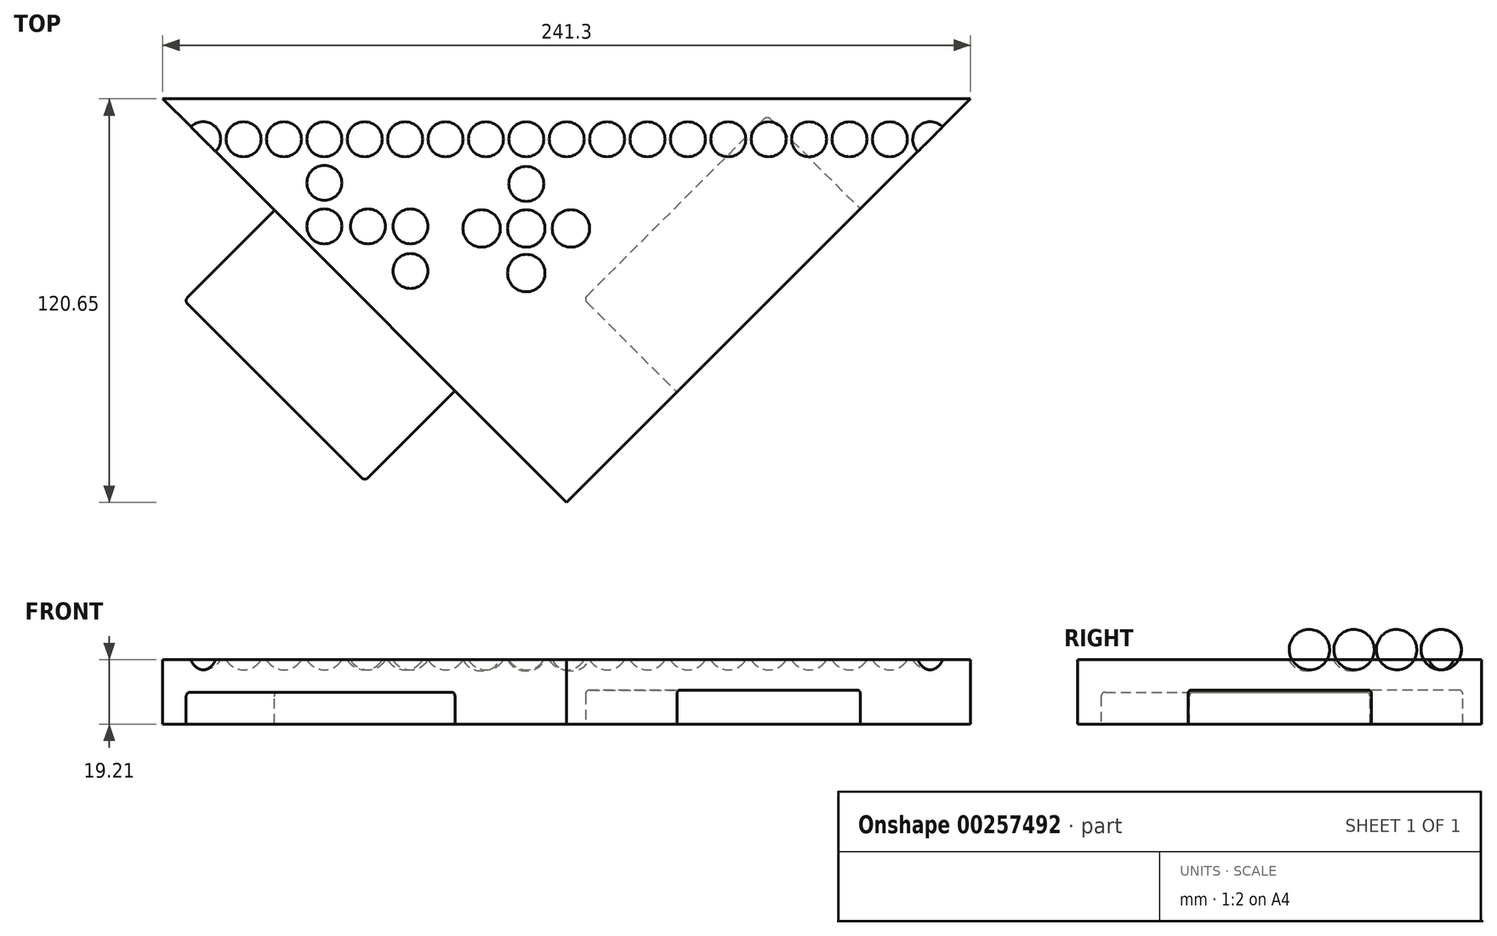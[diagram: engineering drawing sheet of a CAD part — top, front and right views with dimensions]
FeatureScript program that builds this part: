
annotation { "Feature Type Name" : "Feature", "Feature Type Description" : "" }
export const myFeature = defineFeature(function(context is Context, id is Id, definition is map)
    precondition{}
    {
        {
            var Q0;
            Q0=qCreatedBy(makeId("Top.planeOp"),FACE);
            var sketch = newSketch(context, id + "F0", { "sketchPlane" : qUnion([Q0])});
            skLineSegment(sketch, "E0.bottom", {"start": v(120.65, -120.65) * mm, "end": v(-120.65, -120.65) * mm});
            skLineSegment(sketch, "E0.top", {"start": v(120.65, 120.65) * mm, "end": v(-120.65, 120.65) * mm});
            skLineSegment(sketch, "E0.left", {"start": v(120.65, -120.65) * mm, "end": v(120.65, 120.65) * mm});
            skLineSegment(sketch, "E0.right", {"start": v(-120.65, -120.65) * mm, "end": v(-120.65, 120.65) * mm});
            skPoint(sketch, "E0.middle", {"position": v(0, 0) * mm});
            skSolve(sketch);
        }
        {
            var Q0;
            Q0=makeQuery(id+"F0.imprint","IMPRINT",FACE,{"disambiguationData":[TD([[makeQuery(id+"F0.imprint","IMPRINT",EDGE,{"derivedFrom":sQuery(id+"F0.wireOp",EDGE,"E0.bottom")}),-1.0]])]});
            extrude(context, id + "F1", {"entities" : qUnion([Q0]), "depth" : 19.05 * mm});
        }
        {
            var Q0;
            Q0=makeQuery(id+"F1.opExtrude","CAP_FACE",FACE,{"disambiguationData":[OSD([sQuery(id+"F0.wireOp",EDGE,"E0.bottom"),sQuery(id+"F0.wireOp",EDGE,"E0.top"),sQuery(id+"F0.wireOp",EDGE,"E0.left"),sQuery(id+"F0.wireOp",EDGE,"E0.right")])],"isStart":false});
            var sketch = newSketch(context, id + "F2", { "sketchPlane" : qUnion([Q0])});
            skLineSegment(sketch, "E1", {"start": v(120.65, 120.65) * mm, "end": v(0, 0) * mm});
            skLineSegment(sketch, "E2", {"start": v(0, 0) * mm, "end": v(-120.65, 120.65) * mm});
            skLineSegment(sketch, "E3", {"start": v(-120.65, 120.65) * mm, "end": v(-120.65, -120.65) * mm});
            skLineSegment(sketch, "E4", {"start": v(-120.65, -120.65) * mm, "end": v(120.65, -120.65) * mm});
            skLineSegment(sketch, "E5", {"start": v(120.65, -120.65) * mm, "end": v(120.65, 120.65) * mm});
            skSolve(sketch);
        }
        {
            var Q0;
            Q0 = qSketchRegion(id + "F2", true);
            extrude(context, id + "F3", {"entities" : qUnion([Q0]), "operationType" : NewBodyOperationType.REMOVE, "endBound" : BoundingType.THROUGH_ALL, "oppositeDirection" : true, "depth" : 25.4 * mm});
        }
        {
            var Q0;
            Q0=makeQuery(id+"F3.boolean.opBoolean","COPY",FACE,{"derivedFrom":makeQuery(id+"F3.opExtrude","SWEPT_FACE",FACE,{"disambiguationData":[OSD([sQuery(id+"F2.wireOp",EDGE,"E1")])]})});
            var sketch = newSketch(context, id + "F4", { "sketchPlane" : qUnion([Q0])});
            skLineSegment(sketch, "E6.bottom", {"start": v(124.05, 10.16) * mm, "end": v(46.58, 10.16) * mm});
            skLineSegment(sketch, "E6.top", {"start": v(124.05, -10.16) * mm, "end": v(46.58, -10.16) * mm});
            skLineSegment(sketch, "E6.left", {"start": v(124.05, 10.16) * mm, "end": v(124.05, -10.16) * mm});
            skLineSegment(sketch, "E6.right", {"start": v(46.58, 10.16) * mm, "end": v(46.58, -10.16) * mm});
            skPoint(sketch, "E6.middle", {"position": v(85.31, 0) * mm});
            skSolve(sketch);
        }
        {
            var Q0;
            Q0 = qSketchRegion(id + "F4", true);
            extrude(context, id + "F5", {"entities" : qUnion([Q0]), "operationType" : NewBodyOperationType.REMOVE, "oppositeDirection" : true, "depth" : 39.37 * mm});
        }
        {
            var Q0;
            Q0=makeQuery(id+"F3.boolean.opBoolean","COPY",FACE,{"derivedFrom":makeQuery(id+"F3.opExtrude","SWEPT_FACE",FACE,{"disambiguationData":[OSD([sQuery(id+"F2.wireOp",EDGE,"E2")])]})});
            var sketch = newSketch(context, id + "F6", { "sketchPlane" : qUnion([Q0])});
            skLineSegment(sketch, "E7.bottom", {"start": v(-47.21, -9.53) * mm, "end": v(-123.41, -9.52) * mm});
            skLineSegment(sketch, "E7.top", {"start": v(-47.21, 9.52) * mm, "end": v(-123.41, 9.53) * mm});
            skLineSegment(sketch, "E7.left", {"start": v(-47.21, -9.53) * mm, "end": v(-47.21, 9.53) * mm});
            skLineSegment(sketch, "E7.right", {"start": v(-123.41, -9.52) * mm, "end": v(-123.41, 9.53) * mm});
            skPoint(sketch, "E7.middle", {"position": v(-85.31, 0) * mm});
            skSolve(sketch);
        }
        {
            var Q0;
            {var subQ0=sQuery(id+"F6.wireOp",EDGE,"E7.top");Q0=makeQuery(id+"F6.imprint","IMPRINT",FACE,{"disambiguationData":[TD([[makeQuery(id+"F6.imprint","IMPRINT",EDGE,{"derivedFrom":subQ0}),1.0]])]});}
            extrude(context, id + "F7", {"entities" : qUnion([Q0]), "operationType" : NewBodyOperationType.ADD, "depth" : 38.1 * mm});
        }
        {
            var Q0;
            Q0=makeQuery(id+"F7.opExtrude","CAP_EDGE",EDGE,{"disambiguationData":[OSD([sQuery(id+"F6.wireOp",EDGE,"E7.left")])],"isStart":true});
            var Q1;
            Q1=makeQuery(id+"F7.opExtrude","CAP_EDGE",EDGE,{"disambiguationData":[OSD([sQuery(id+"F6.wireOp",EDGE,"E7.top")])],"isStart":true});
            var Q2;
            Q2=makeQuery(id+"F7.opExtrude","CAP_EDGE",EDGE,{"disambiguationData":[OSD([sQuery(id+"F6.wireOp",EDGE,"E7.right")])],"isStart":true});
            var Q3;
            Q3=makeQuery(id+"F5.boolean.opBoolean","COPY",EDGE,{"derivedFrom":makeQuery(id+"F5.opExtrude","CAP_EDGE",EDGE,{"disambiguationData":[OSD([sQuery(id+"F4.wireOp",EDGE,"E6.right")])],"isStart":false})});
            var Q4;
            Q4=makeQuery(id+"F5.boolean.opBoolean","COPY",EDGE,{"derivedFrom":makeQuery(id+"F5.opExtrude","CAP_EDGE",EDGE,{"disambiguationData":[OSD([sQuery(id+"F4.wireOp",EDGE,"E6.bottom")])],"isStart":false})});
            var Q5;
            Q5=makeQuery(id+"F5.boolean.opBoolean","COPY",EDGE,{"derivedFrom":makeQuery(id+"F5.opExtrude","CAP_EDGE",EDGE,{"disambiguationData":[OSD([sQuery(id+"F4.wireOp",EDGE,"E6.left")])],"isStart":false})});
            var Q6;
            Q6=makeQuery(id+"F5.boolean.opBoolean","COPY",EDGE,{"derivedFrom":makeQuery(id+"F5.opExtrude","SWEPT_EDGE",EDGE,{"disambiguationData":[OSD([sQuery(id+"F4.wireOp",EDGE,"E6.bottom"),sQuery(id+"F4.wireOp",EDGE,"E6.left")])]})});
            var Q7;
            Q7=makeQuery(id+"F5.boolean.opBoolean","COPY",EDGE,{"derivedFrom":makeQuery(id+"F5.opExtrude","SWEPT_EDGE",EDGE,{"disambiguationData":[OSD([sQuery(id+"F4.wireOp",EDGE,"E6.bottom"),sQuery(id+"F4.wireOp",EDGE,"E6.right")])]})});
            fillet(context, id + "F8", {"entities" : qUnion([Q0, Q1, Q2, Q3, Q4, Q5, Q6, Q7]), "radius" : 1.27 * mm, "tangentPropagation" : true, "allowEdgeOverflow" : false});
        }
        {
            var Q0;
            Q0=makeQuery(id+"F7.opExtrude","SWEPT_EDGE",EDGE,{"disambiguationData":[OSD([sQuery(id+"F6.wireOp",EDGE,"E7.top"),sQuery(id+"F6.wireOp",EDGE,"E7.left")])]});
            var Q1;
            Q1=makeQuery(id+"F7.opExtrude","CAP_EDGE",EDGE,{"disambiguationData":[OSD([sQuery(id+"F6.wireOp",EDGE,"E7.left")])],"isStart":false});
            var Q2;
            Q2=makeQuery(id+"F7.opExtrude","CAP_EDGE",EDGE,{"disambiguationData":[OSD([sQuery(id+"F6.wireOp",EDGE,"E7.top")])],"isStart":false});
            var Q3;
            Q3=makeQuery(id+"F7.opExtrude","CAP_EDGE",EDGE,{"disambiguationData":[OSD([sQuery(id+"F6.wireOp",EDGE,"E7.right")])],"isStart":false});
            var Q4;
            Q4=makeQuery(id+"F7.opExtrude","SWEPT_EDGE",EDGE,{"disambiguationData":[OSD([sQuery(id+"F6.wireOp",EDGE,"E7.top"),sQuery(id+"F6.wireOp",EDGE,"E7.right")])]});
            var Q5;
            Q5=makeQuery(id+"F5.boolean.opBoolean","COPY",EDGE,{"derivedFrom":makeQuery(id+"F5.opExtrude","CAP_EDGE",EDGE,{"disambiguationData":[OSD([sQuery(id+"F4.wireOp",EDGE,"E6.left")])],"isStart":true})});
            fillet(context, id + "F9", {"entities" : qUnion([Q0, Q1, Q2, Q3, Q4, Q5]), "radius" : 1.27 * mm, "tangentPropagation" : true, "allowEdgeOverflow" : false});
        }
        {
            var Q0;
            Q0=makeQuery(id+"F1.opExtrude","CAP_FACE",FACE,{"disambiguationData":[OSD([sQuery(id+"F0.wireOp",EDGE,"E0.bottom"),sQuery(id+"F0.wireOp",EDGE,"E0.top"),sQuery(id+"F0.wireOp",EDGE,"E0.left"),sQuery(id+"F0.wireOp",EDGE,"E0.right")])],"isStart":false});
            var sketch = newSketch(context, id + "F10", { "sketchPlane" : qUnion([Q0])});
            skLineSegment(sketch, "E8", {"start": v(-120.65, 120.65) * mm, "end": v(120.65, 120.65) * mm});
            skLineSegment(sketch, "E9", {"start": v(120.65, 120.65) * mm, "end": v(0, 0) * mm});
            skLineSegment(sketch, "E10", {"start": v(0, 0) * mm, "end": v(-120.65, 120.65) * mm});
            skSolve(sketch);
        }
        {
            var Q0;
            Q0 = qSketchRegion(id + "F10", true);
            extrude(context, id + "F11", {"entities" : qUnion([Q0]), "operationType" : NewBodyOperationType.ADD, "depth" : 3.17 * mm});
        }
        {
            var Q0;
            Q0=makeQuery(id+"F11.opExtrude","CAP_FACE",FACE,{"disambiguationData":[OSD([sQuery(id+"F10.wireOp",EDGE,"E8"),sQuery(id+"F10.wireOp",EDGE,"E9"),sQuery(id+"F10.wireOp",EDGE,"E10")])],"isStart":false});
            var sketch = newSketch(context, id + "F12", { "sketchPlane" : qUnion([Q0])});
            skCircle(sketch, "E11", {"center": v(0, 111.12) * mm, "radius": 6.35 * mm});
            skSolve(sketch);
        }
        {
            var Q0;
            Q0=makeQuery(id+"F12.imprint","IMPRINT",FACE,{"disambiguationData":[TD([[makeQuery(id+"F12.imprint","IMPRINT",EDGE,{"derivedFrom":sQuery(id+"F12.wireOp",EDGE,"E11")}),-1.0]])]});
            var sketch = newSketch(context, id + "F13", { "sketchPlane" : qUnion([Q0])});
            skLineSegment(sketch, "E12", {"start": v(0, 120.94) * mm, "end": v(0, 0) * mm});
            skSolve(sketch);
        }
        {
            var Q0;
            {var subQ0=makeQuery(id+"F12.imprint","IMPRINT",EDGE,{"derivedFrom":makeQuery(id+"F11.opExtrude","CAP_EDGE",EDGE,{"disambiguationData":[OSD([sQuery(id+"F10.wireOp",EDGE,"E9")])],"isStart":false})});Q0=makeQuery(id+"F13.imprint","IMPRINT",FACE,{"disambiguationData":[TD([[makeQuery(id+"F13.imprint","IMPRINT",EDGE,{"derivedFrom":subQ0}),-1.0]])]});}
            var sketch = newSketch(context, id + "F14", { "sketchPlane" : qUnion([Q0])});
            skArc(sketch, "E13", {"start": v(0, 114.59) * mm, "mid": v(6.03, 108.56) * mm, "end": v(0, 102.52) * mm});
            skLineSegment(sketch, "E14", {"start": v(0, 114.59) * mm, "end": v(0, 102.52) * mm});
            skSolve(sketch);
        }
        {
            var Q0;
            Q0 = qSketchRegion(id + "F14", true);
            var Q1;
            Q1=sQuery(id+"F14.wireOp",EDGE,"E14");
            revolve(context, id + "F15", {"operationType" : NewBodyOperationType.REMOVE, "entities" : qUnion([Q0]), "axis" : qUnion([Q1]), "revolveType" : RevolveType.FULL, "oppositeDirection" : true});
        }
        {
            var Q0;
            Q0=makeQuery(id+"F11.opExtrude","CAP_FACE",FACE,{"disambiguationData":[OSD([sQuery(id+"F10.wireOp",EDGE,"E8"),sQuery(id+"F10.wireOp",EDGE,"E9"),sQuery(id+"F10.wireOp",EDGE,"E10")])],"isStart":false});
            var sketch = newSketch(context, id + "F16", { "sketchPlane" : qUnion([Q0])});
            skLineSegment(sketch, "E15", {"start": v(0, 108.56) * mm, "end": v(-6.03, 108.56) * mm});
            skLineSegment(sketch, "E16", {"start": v(-6.03, 108.56) * mm, "end": v(-18.1, 108.56) * mm});
            skArc(sketch, "E17", {"start": v(-18.1, 108.56) * mm, "mid": v(-12.07, 114.59) * mm, "end": v(-6.03, 108.56) * mm});
            skSolve(sketch);
        }
        {
            var Q0;
            Q0=makeQuery(id+"F16.imprint","IMPRINT",FACE,{"disambiguationData":[TD([[makeQuery(id+"F16.imprint","IMPRINT",EDGE,{"derivedFrom":sQuery(id+"F16.wireOp",EDGE,"E16")}),-1.0]])]});
            var Q1;
            Q1=sQuery(id+"F16.wireOp",EDGE,"E16");
            revolve(context, id + "F17", {"operationType" : NewBodyOperationType.REMOVE, "entities" : qUnion([Q0]), "axis" : qUnion([Q1]), "revolveType" : RevolveType.FULL, "oppositeDirection" : true});
        }
        {
            var Q0;
            Q0=makeQuery(id+"F11.opExtrude","CAP_FACE",FACE,{"disambiguationData":[OSD([sQuery(id+"F10.wireOp",EDGE,"E8"),sQuery(id+"F10.wireOp",EDGE,"E9"),sQuery(id+"F10.wireOp",EDGE,"E10")])],"isStart":false});
            var sketch = newSketch(context, id + "F18", { "sketchPlane" : qUnion([Q0])});
            skLineSegment(sketch, "E18", {"start": v(-11.75, 108.56) * mm, "end": v(-18.1, 108.56) * mm});
            skLineSegment(sketch, "E19", {"start": v(-18.1, 108.56) * mm, "end": v(-30.16, 108.56) * mm});
            skArc(sketch, "E20", {"start": v(-30.16, 108.56) * mm, "mid": v(-24.13, 114.59) * mm, "end": v(-18.1, 108.56) * mm});
            skSolve(sketch);
        }
        {
            var Q0;
            Q0=makeQuery(id+"F16.imprint","IMPRINT",FACE,{"disambiguationData":[TD([[makeQuery(id+"F16.imprint","IMPRINT",EDGE,{"derivedFrom":sQuery(id+"F16.wireOp",EDGE,"E16")}),1.0]])]});
            var sketch = newSketch(context, id + "F19", { "sketchPlane" : qUnion([Q0])});
            skLineSegment(sketch, "E21", {"start": v(-30.16, 108.56) * mm, "end": v(-42.23, 108.56) * mm});
            skArc(sketch, "E22", {"start": v(-42.23, 108.56) * mm, "mid": v(-36.2, 114.59) * mm, "end": v(-30.16, 108.56) * mm});
            skSolve(sketch);
        }
        {
            var Q0;
            Q0 = qSketchRegion(id + "F18", true);
            var Q1;
            Q1 = qSketchRegion(id + "F19", true);
            var Q2;
            Q2=sQuery(id+"F19.wireOp",EDGE,"E21");
            revolve(context, id + "F20", {"operationType" : NewBodyOperationType.REMOVE, "entities" : qUnion([Q0, Q1]), "axis" : qUnion([Q2]), "revolveType" : RevolveType.FULL, "oppositeDirection" : true});
        }
        {
            var Q0;
            Q0=makeQuery(id+"F16.imprint","IMPRINT",FACE,{"disambiguationData":[TD([[makeQuery(id+"F16.imprint","IMPRINT",EDGE,{"derivedFrom":sQuery(id+"F16.wireOp",EDGE,"E16")}),1.0]])]});
            var sketch = newSketch(context, id + "F21", { "sketchPlane" : qUnion([Q0])});
            skLineSegment(sketch, "E23", {"start": v(-42.23, 108.56) * mm, "end": v(-54.3, 108.56) * mm});
            skArc(sketch, "E24", {"start": v(-54.3, 108.56) * mm, "mid": v(-48.26, 114.59) * mm, "end": v(-42.23, 108.56) * mm});
            skSolve(sketch);
        }
        {
            var Q0;
            Q0=makeQuery(id+"F16.imprint","IMPRINT",FACE,{"disambiguationData":[TD([[makeQuery(id+"F16.imprint","IMPRINT",EDGE,{"derivedFrom":sQuery(id+"F16.wireOp",EDGE,"E16")}),1.0]])]});
            var sketch = newSketch(context, id + "F22", { "sketchPlane" : qUnion([Q0])});
            skLineSegment(sketch, "E25", {"start": v(-54.3, 108.56) * mm, "end": v(-66.36, 108.56) * mm});
            skArc(sketch, "E26", {"start": v(-66.36, 108.56) * mm, "mid": v(-60.32, 114.59) * mm, "end": v(-54.3, 108.56) * mm});
            skSolve(sketch);
        }
        {
            var Q0;
            Q0=makeQuery(id+"F16.imprint","IMPRINT",FACE,{"disambiguationData":[TD([[makeQuery(id+"F16.imprint","IMPRINT",EDGE,{"derivedFrom":sQuery(id+"F16.wireOp",EDGE,"E16")}),1.0]])]});
            var sketch = newSketch(context, id + "F23", { "sketchPlane" : qUnion([Q0])});
            skLineSegment(sketch, "E27", {"start": v(-66.36, 108.56) * mm, "end": v(-78.42, 108.56) * mm});
            skArc(sketch, "E28", {"start": v(-78.42, 108.56) * mm, "mid": v(-72.4, 114.59) * mm, "end": v(-66.36, 108.56) * mm});
            skSolve(sketch);
        }
        {
            var Q0;
            Q0=makeQuery(id+"F19.imprint","IMPRINT",FACE,{"disambiguationData":[TD([[makeQuery(id+"F19.imprint","IMPRINT",EDGE,{"derivedFrom":sQuery(id+"F19.wireOp",EDGE,"E21")}),1.0]])]});
            var sketch = newSketch(context, id + "F24", { "sketchPlane" : qUnion([Q0])});
            skLineSegment(sketch, "E29", {"start": v(-78.42, 108.56) * mm, "end": v(-90.49, 108.56) * mm});
            skArc(sketch, "E30", {"start": v(-90.49, 108.56) * mm, "mid": v(-84.46, 114.59) * mm, "end": v(-78.42, 108.56) * mm});
            skSolve(sketch);
        }
        {
            var Q0;
            {var subQ0=makeQuery(id+"F12.imprint","IMPRINT",EDGE,{"derivedFrom":makeQuery(id+"F11.opExtrude","CAP_EDGE",EDGE,{"disambiguationData":[OSD([sQuery(id+"F10.wireOp",EDGE,"E9")])],"isStart":false})});Q0=makeQuery(id+"F14.imprint","IMPRINT",FACE,{"disambiguationData":[TD([[makeQuery(id+"F14.imprint","IMPRINT",EDGE,{"derivedFrom":makeQuery(id+"F13.imprint","IMPRINT",EDGE,{"derivedFrom":subQ0})}),-1.0]])]});}
            var sketch = newSketch(context, id + "F25", { "sketchPlane" : qUnion([Q0])});
            skLineSegment(sketch, "E31", {"start": v(-90.49, 108.56) * mm, "end": v(-102.55, 108.56) * mm});
            skArc(sketch, "E32", {"start": v(-102.55, 108.56) * mm, "mid": v(-96.52, 114.59) * mm, "end": v(-90.49, 108.56) * mm});
            skSolve(sketch);
        }
        {
            var Q0;
            Q0=makeQuery(id+"F24.imprint","IMPRINT",FACE,{"disambiguationData":[TD([[makeQuery(id+"F24.imprint","IMPRINT",EDGE,{"derivedFrom":sQuery(id+"F24.wireOp",EDGE,"E29")}),1.0]])]});
            var sketch = newSketch(context, id + "F26", { "sketchPlane" : qUnion([Q0])});
            skLineSegment(sketch, "E33", {"start": v(-102.55, 108.56) * mm, "end": v(-114.62, 108.56) * mm});
            skArc(sketch, "E34", {"start": v(-114.62, 108.56) * mm, "mid": v(-108.59, 114.59) * mm, "end": v(-102.55, 108.56) * mm});
            skSolve(sketch);
        }
        {
            var Q0;
            Q0 = qSketchRegion(id + "F21", true);
            var Q1;
            Q1 = qSketchRegion(id + "F22", true);
            var Q2;
            Q2 = qSketchRegion(id + "F23", true);
            var Q3;
            Q3 = qSketchRegion(id + "F24", true);
            var Q4;
            Q4 = qSketchRegion(id + "F25", true);
            var Q5;
            Q5 = qSketchRegion(id + "F26", true);
            var Q6;
            Q6=sQuery(id+"F21.wireOp",EDGE,"E23");
            revolve(context, id + "F27", {"operationType" : NewBodyOperationType.REMOVE, "entities" : qUnion([Q0, Q1, Q2, Q3, Q4, Q5]), "axis" : qUnion([Q6]), "revolveType" : RevolveType.FULL, "oppositeDirection" : true});
        }
        {
            var Q0;
            Q0=makeQuery(id+"F19.imprint","IMPRINT",FACE,{"disambiguationData":[TD([[makeQuery(id+"F19.imprint","IMPRINT",EDGE,{"derivedFrom":sQuery(id+"F19.wireOp",EDGE,"E21")}),1.0]])]});
            var sketch = newSketch(context, id + "F28", { "sketchPlane" : qUnion([Q0])});
            skLineSegment(sketch, "E35", {"start": v(6.03, 108.56) * mm, "end": v(18.1, 108.56) * mm});
            skArc(sketch, "E36", {"start": v(6.03, 108.56) * mm, "mid": v(12.07, 114.59) * mm, "end": v(18.1, 108.56) * mm});
            skSolve(sketch);
        }
        {
            var Q0;
            Q0=makeQuery(id+"F19.imprint","IMPRINT",FACE,{"disambiguationData":[TD([[makeQuery(id+"F19.imprint","IMPRINT",EDGE,{"derivedFrom":sQuery(id+"F19.wireOp",EDGE,"E21")}),1.0]])]});
            var sketch = newSketch(context, id + "F29", { "sketchPlane" : qUnion([Q0])});
            skLineSegment(sketch, "E37", {"start": v(18.1, 108.56) * mm, "end": v(30.16, 108.56) * mm});
            skArc(sketch, "E38", {"start": v(18.1, 108.56) * mm, "mid": v(24.13, 114.59) * mm, "end": v(30.16, 108.56) * mm});
            skSolve(sketch);
        }
        {
            var Q0;
            Q0=makeQuery(id+"F19.imprint","IMPRINT",FACE,{"disambiguationData":[TD([[makeQuery(id+"F19.imprint","IMPRINT",EDGE,{"derivedFrom":sQuery(id+"F19.wireOp",EDGE,"E21")}),1.0]])]});
            var sketch = newSketch(context, id + "F30", { "sketchPlane" : qUnion([Q0])});
            skLineSegment(sketch, "E39", {"start": v(42.23, 108.56) * mm, "end": v(30.16, 108.56) * mm});
            skArc(sketch, "E40", {"start": v(30.16, 108.56) * mm, "mid": v(36.2, 114.59) * mm, "end": v(42.23, 108.56) * mm});
            skSolve(sketch);
        }
        {
            var Q0;
            Q0=makeQuery(id+"F19.imprint","IMPRINT",FACE,{"disambiguationData":[TD([[makeQuery(id+"F19.imprint","IMPRINT",EDGE,{"derivedFrom":sQuery(id+"F19.wireOp",EDGE,"E21")}),1.0]])]});
            var sketch = newSketch(context, id + "F31", { "sketchPlane" : qUnion([Q0])});
            skLineSegment(sketch, "E41", {"start": v(42.23, 108.56) * mm, "end": v(54.3, 108.56) * mm});
            skArc(sketch, "E42", {"start": v(42.23, 108.56) * mm, "mid": v(48.26, 114.59) * mm, "end": v(54.3, 108.56) * mm});
            skSolve(sketch);
        }
        {
            var Q0;
            Q0=makeQuery(id+"F19.imprint","IMPRINT",FACE,{"disambiguationData":[TD([[makeQuery(id+"F19.imprint","IMPRINT",EDGE,{"derivedFrom":sQuery(id+"F19.wireOp",EDGE,"E21")}),1.0]])]});
            var sketch = newSketch(context, id + "F32", { "sketchPlane" : qUnion([Q0])});
            skLineSegment(sketch, "E43", {"start": v(66.36, 108.56) * mm, "end": v(54.3, 108.56) * mm});
            skArc(sketch, "E44", {"start": v(54.3, 108.56) * mm, "mid": v(60.33, 114.59) * mm, "end": v(66.36, 108.56) * mm});
            skSolve(sketch);
        }
        {
            var Q0;
            Q0=makeQuery(id+"F19.imprint","IMPRINT",FACE,{"disambiguationData":[TD([[makeQuery(id+"F19.imprint","IMPRINT",EDGE,{"derivedFrom":sQuery(id+"F19.wireOp",EDGE,"E21")}),1.0]])]});
            var sketch = newSketch(context, id + "F33", { "sketchPlane" : qUnion([Q0])});
            skLineSegment(sketch, "E45", {"start": v(78.42, 108.56) * mm, "end": v(66.36, 108.56) * mm});
            skArc(sketch, "E46", {"start": v(66.36, 108.56) * mm, "mid": v(72.4, 114.59) * mm, "end": v(78.42, 108.56) * mm});
            skSolve(sketch);
        }
        {
            var Q0;
            Q0=makeQuery(id+"F19.imprint","IMPRINT",FACE,{"disambiguationData":[TD([[makeQuery(id+"F19.imprint","IMPRINT",EDGE,{"derivedFrom":sQuery(id+"F19.wireOp",EDGE,"E21")}),1.0]])]});
            var sketch = newSketch(context, id + "F34", { "sketchPlane" : qUnion([Q0])});
            skLineSegment(sketch, "E47", {"start": v(90.49, 108.56) * mm, "end": v(78.42, 108.56) * mm});
            skArc(sketch, "E48", {"start": v(78.42, 108.56) * mm, "mid": v(84.45, 114.59) * mm, "end": v(90.49, 108.56) * mm});
            skSolve(sketch);
        }
        {
            var Q0;
            Q0=makeQuery(id+"F19.imprint","IMPRINT",FACE,{"disambiguationData":[TD([[makeQuery(id+"F19.imprint","IMPRINT",EDGE,{"derivedFrom":sQuery(id+"F19.wireOp",EDGE,"E21")}),1.0]])]});
            var sketch = newSketch(context, id + "F35", { "sketchPlane" : qUnion([Q0])});
            skLineSegment(sketch, "E49", {"start": v(102.55, 108.56) * mm, "end": v(90.49, 108.56) * mm});
            skArc(sketch, "E50", {"start": v(90.49, 108.56) * mm, "mid": v(96.52, 114.59) * mm, "end": v(102.55, 108.56) * mm});
            skSolve(sketch);
        }
        {
            var Q0;
            Q0=makeQuery(id+"F19.imprint","IMPRINT",FACE,{"disambiguationData":[TD([[makeQuery(id+"F19.imprint","IMPRINT",EDGE,{"derivedFrom":sQuery(id+"F19.wireOp",EDGE,"E21")}),1.0]])]});
            var sketch = newSketch(context, id + "F36", { "sketchPlane" : qUnion([Q0])});
            skLineSegment(sketch, "E51", {"start": v(114.62, 108.56) * mm, "end": v(102.55, 108.56) * mm});
            skArc(sketch, "E52", {"start": v(102.55, 108.56) * mm, "mid": v(108.58, 114.59) * mm, "end": v(114.62, 108.56) * mm});
            skSolve(sketch);
        }
        {
            var Q0;
            Q0 = qSketchRegion(id + "F28", true);
            var Q1;
            Q1 = qSketchRegion(id + "F29", true);
            var Q2;
            Q2 = qSketchRegion(id + "F30", true);
            var Q3;
            Q3 = qSketchRegion(id + "F31", true);
            var Q4;
            Q4 = qSketchRegion(id + "F32", true);
            var Q5;
            Q5 = qSketchRegion(id + "F33", true);
            var Q6;
            Q6 = qSketchRegion(id + "F34", true);
            var Q7;
            Q7 = qSketchRegion(id + "F35", true);
            var Q8;
            Q8 = qSketchRegion(id + "F36", true);
            var Q9;
            Q9=sQuery(id+"F28.wireOp",EDGE,"E35");
            revolve(context, id + "F37", {"operationType" : NewBodyOperationType.REMOVE, "entities" : qUnion([Q0, Q1, Q2, Q3, Q4, Q5, Q6, Q7, Q8]), "axis" : qUnion([Q9]), "revolveType" : RevolveType.FULL, "oppositeDirection" : true});
        }
        {
            var Q0;
            Q0=makeQuery(id+"F11.boolean.opBoolean","MERGE",FACE,{"derivedFrom":[makeQuery(id+"F1.opExtrude","SWEPT_FACE",FACE,{"disambiguationData":[OSD([sQuery(id+"F0.wireOp",EDGE,"E0.top")])]}),makeQuery(id+"F11.opExtrude","SWEPT_FACE",FACE,{"disambiguationData":[OSD([sQuery(id+"F10.wireOp",EDGE,"E8")])]})]});
            var sketch = newSketch(context, id + "F38", { "sketchPlane" : qUnion([Q0])});
            skLineSegment(sketch, "E53.bottom", {"start": v(-146.05, 19.2) * mm, "end": v(158.75, 19.2) * mm});
            skLineSegment(sketch, "E53.top", {"start": v(-146.05, 27.73) * mm, "end": v(158.75, 27.73) * mm});
            skLineSegment(sketch, "E53.left", {"start": v(-146.05, 19.2) * mm, "end": v(-146.05, 27.73) * mm});
            skLineSegment(sketch, "E53.right", {"start": v(158.75, 19.2) * mm, "end": v(158.75, 27.73) * mm});
            skSolve(sketch);
        }
        {
            var Q0;
            Q0=makeQuery(id+"F23.imprint","IMPRINT",FACE,{"disambiguationData":[TD([[makeQuery(id+"F23.imprint","IMPRINT",EDGE,{"derivedFrom":sQuery(id+"F23.wireOp",EDGE,"E27")}),1.0]])]});
            var sketch = newSketch(context, id + "F39", { "sketchPlane" : qUnion([Q0])});
            skLineSegment(sketch, "E54", {"start": v(-72.4, 101.57) * mm, "end": v(-72.4, 89.5) * mm});
            skArc(sketch, "E55", {"start": v(-72.4, 89.5) * mm, "mid": v(-66.36, 95.54) * mm, "end": v(-72.4, 101.57) * mm});
            skSolve(sketch);
        }
        {
            var Q0;
            Q0=makeQuery(id+"F23.imprint","IMPRINT",FACE,{"disambiguationData":[TD([[makeQuery(id+"F23.imprint","IMPRINT",EDGE,{"derivedFrom":sQuery(id+"F23.wireOp",EDGE,"E27")}),1.0]])]});
            var sketch = newSketch(context, id + "F40", { "sketchPlane" : qUnion([Q0])});
            skLineSegment(sketch, "E56", {"start": v(-72.4, 88.55) * mm, "end": v(-72.4, 76.49) * mm});
            skArc(sketch, "E57", {"start": v(-72.4, 76.49) * mm, "mid": v(-66.36, 82.52) * mm, "end": v(-72.4, 88.55) * mm});
            skSolve(sketch);
        }
        {
            var Q0;
            Q0 = qSketchRegion(id + "F39", true);
            var Q1;
            Q1 = qSketchRegion(id + "F40", true);
            var Q2;
            Q2=sQuery(id+"F39.wireOp",EDGE,"E54");
            revolve(context, id + "F41", {"operationType" : NewBodyOperationType.REMOVE, "entities" : qUnion([Q0, Q1]), "axis" : qUnion([Q2]), "revolveType" : RevolveType.FULL, "oppositeDirection" : true});
        }
        {
            var Q0;
            Q0=makeQuery(id+"F23.imprint","IMPRINT",FACE,{"disambiguationData":[TD([[makeQuery(id+"F23.imprint","IMPRINT",EDGE,{"derivedFrom":sQuery(id+"F23.wireOp",EDGE,"E27")}),1.0]])]});
            var sketch = newSketch(context, id + "F42", { "sketchPlane" : qUnion([Q0])});
            skLineSegment(sketch, "E58", {"start": v(-65.4, 82.52) * mm, "end": v(-53.34, 82.52) * mm});
            skArc(sketch, "E59", {"start": v(-65.4, 82.52) * mm, "mid": v(-59.37, 76.49) * mm, "end": v(-53.34, 82.52) * mm});
            skSolve(sketch);
        }
        {
            var Q0;
            Q0=makeQuery(id+"F23.imprint","IMPRINT",FACE,{"disambiguationData":[TD([[makeQuery(id+"F23.imprint","IMPRINT",EDGE,{"derivedFrom":sQuery(id+"F23.wireOp",EDGE,"E27")}),1.0]])]});
            var sketch = newSketch(context, id + "F43", { "sketchPlane" : qUnion([Q0])});
            skLineSegment(sketch, "E60", {"start": v(-52.7, 82.52) * mm, "end": v(-40.64, 82.52) * mm});
            skArc(sketch, "E61", {"start": v(-52.7, 82.52) * mm, "mid": v(-46.67, 88.55) * mm, "end": v(-40.64, 82.52) * mm});
            skSolve(sketch);
        }
        {
            var Q0;
            Q0=makeQuery(id+"F23.imprint","IMPRINT",FACE,{"disambiguationData":[TD([[makeQuery(id+"F23.imprint","IMPRINT",EDGE,{"derivedFrom":sQuery(id+"F23.wireOp",EDGE,"E27")}),1.0]])]});
            var sketch = newSketch(context, id + "F44", { "sketchPlane" : qUnion([Q0])});
            skLineSegment(sketch, "E62", {"start": v(-52.7, 69.19) * mm, "end": v(-40.64, 69.19) * mm});
            skArc(sketch, "E63", {"start": v(-52.7, 69.19) * mm, "mid": v(-46.67, 75.22) * mm, "end": v(-40.64, 69.19) * mm});
            skSolve(sketch);
        }
        {
            var Q0;
            Q0 = qSketchRegion(id + "F42", true);
            var Q1;
            Q1 = qSketchRegion(id + "F43", true);
            var Q2;
            Q2=sQuery(id+"F42.wireOp",EDGE,"E58");
            revolve(context, id + "F45", {"operationType" : NewBodyOperationType.REMOVE, "entities" : qUnion([Q0, Q1]), "axis" : qUnion([Q2]), "revolveType" : RevolveType.FULL, "oppositeDirection" : true});
        }
        {
            var Q0;
            Q0 = qSketchRegion(id + "F44", true);
            var Q1;
            Q1=sQuery(id+"F44.wireOp",EDGE,"E62");
            revolve(context, id + "F46", {"operationType" : NewBodyOperationType.REMOVE, "entities" : qUnion([Q0]), "axis" : qUnion([Q1]), "revolveType" : RevolveType.FULL, "oppositeDirection" : true});
        }
        {
            var Q0;
            Q0=makeQuery(id+"F23.imprint","IMPRINT",FACE,{"disambiguationData":[TD([[makeQuery(id+"F23.imprint","IMPRINT",EDGE,{"derivedFrom":sQuery(id+"F23.wireOp",EDGE,"E27")}),1.0]])]});
            var sketch = newSketch(context, id + "F47", { "sketchPlane" : qUnion([Q0])});
            skLineSegment(sketch, "E64", {"start": v(-6.03, 95.22) * mm, "end": v(-18.1, 95.22) * mm});
            skArc(sketch, "E65", {"start": v(-18.1, 95.22) * mm, "mid": v(-12.07, 101.25) * mm, "end": v(-6.03, 95.22) * mm});
            skSolve(sketch);
        }
        {
            var Q0;
            Q0=makeQuery(id+"F16.imprint","IMPRINT",FACE,{"disambiguationData":[TD([[makeQuery(id+"F16.imprint","IMPRINT",EDGE,{"derivedFrom":sQuery(id+"F16.wireOp",EDGE,"E16")}),1.0]])]});
            var sketch = newSketch(context, id + "F48", { "sketchPlane" : qUnion([Q0])});
            skLineSegment(sketch, "E66", {"start": v(-18.42, 81.89) * mm, "end": v(-5.72, 81.89) * mm});
            skArc(sketch, "E67", {"start": v(-18.42, 81.89) * mm, "mid": v(-12.07, 88.24) * mm, "end": v(-5.72, 81.89) * mm});
            skSolve(sketch);
        }
        {
            var Q0;
            Q0=makeQuery(id+"F16.imprint","IMPRINT",FACE,{"disambiguationData":[TD([[makeQuery(id+"F16.imprint","IMPRINT",EDGE,{"derivedFrom":sQuery(id+"F16.wireOp",EDGE,"E16")}),1.0]])]});
            var sketch = newSketch(context, id + "F49", { "sketchPlane" : qUnion([Q0])});
            skLineSegment(sketch, "E68", {"start": v(-18.42, 68.55) * mm, "end": v(-5.72, 68.55) * mm});
            skArc(sketch, "E69", {"start": v(-5.72, 68.55) * mm, "mid": v(-12.07, 74.9) * mm, "end": v(-18.42, 68.55) * mm});
            skSolve(sketch);
        }
        {
            var Q0;
            Q0=makeQuery(id+"F16.imprint","IMPRINT",FACE,{"disambiguationData":[TD([[makeQuery(id+"F16.imprint","IMPRINT",EDGE,{"derivedFrom":sQuery(id+"F16.wireOp",EDGE,"E16")}),1.0]])]});
            var sketch = newSketch(context, id + "F50", { "sketchPlane" : qUnion([Q0])});
            skLineSegment(sketch, "E70", {"start": v(-5.08, 81.89) * mm, "end": v(7.62, 81.89) * mm});
            skArc(sketch, "E71", {"start": v(-5.08, 81.89) * mm, "mid": v(1.27, 88.24) * mm, "end": v(7.62, 81.89) * mm});
            skSolve(sketch);
        }
        {
            var Q0;
            Q0=makeQuery(id+"F16.imprint","IMPRINT",FACE,{"disambiguationData":[TD([[makeQuery(id+"F16.imprint","IMPRINT",EDGE,{"derivedFrom":sQuery(id+"F16.wireOp",EDGE,"E16")}),1.0]])]});
            var sketch = newSketch(context, id + "F51", { "sketchPlane" : qUnion([Q0])});
            skLineSegment(sketch, "E72", {"start": v(-19.05, 81.89) * mm, "end": v(-31.75, 81.89) * mm});
            skArc(sketch, "E73", {"start": v(-31.75, 81.89) * mm, "mid": v(-25.4, 88.24) * mm, "end": v(-19.05, 81.89) * mm});
            skSolve(sketch);
        }
        {
            var Q0;
            Q0 = qSketchRegion(id + "F51", true);
            var Q1;
            Q1 = qSketchRegion(id + "F50", true);
            var Q2;
            Q2 = qSketchRegion(id + "F48", true);
            var Q3;
            Q3=sQuery(id+"F50.wireOp",EDGE,"E70");
            revolve(context, id + "F52", {"operationType" : NewBodyOperationType.REMOVE, "entities" : qUnion([Q0, Q1, Q2]), "axis" : qUnion([Q3]), "revolveType" : RevolveType.FULL, "oppositeDirection" : true});
        }
        {
            var Q0;
            Q0 = qSketchRegion(id + "F47", true);
            var Q1;
            Q1=sQuery(id+"F47.wireOp",EDGE,"E64");
            revolve(context, id + "F53", {"operationType" : NewBodyOperationType.REMOVE, "entities" : qUnion([Q0]), "axis" : qUnion([Q1]), "revolveType" : RevolveType.FULL, "oppositeDirection" : true});
        }
        {
            var Q0;
            Q0 = qSketchRegion(id + "F49", true);
            var Q1;
            Q1=sQuery(id+"F49.wireOp",EDGE,"E68");
            revolve(context, id + "F54", {"operationType" : NewBodyOperationType.REMOVE, "entities" : qUnion([Q0]), "axis" : qUnion([Q1]), "revolveType" : RevolveType.FULL, "oppositeDirection" : true});
        }
        {
            var Q0;
            Q0 = qSketchRegion(id + "F38", true);
            extrude(context, id + "F55", {"entities" : qUnion([Q0]), "operationType" : NewBodyOperationType.REMOVE, "endBound" : BoundingType.THROUGH_ALL, "oppositeDirection" : true, "depth" : 25.4 * mm});
        }
    });
